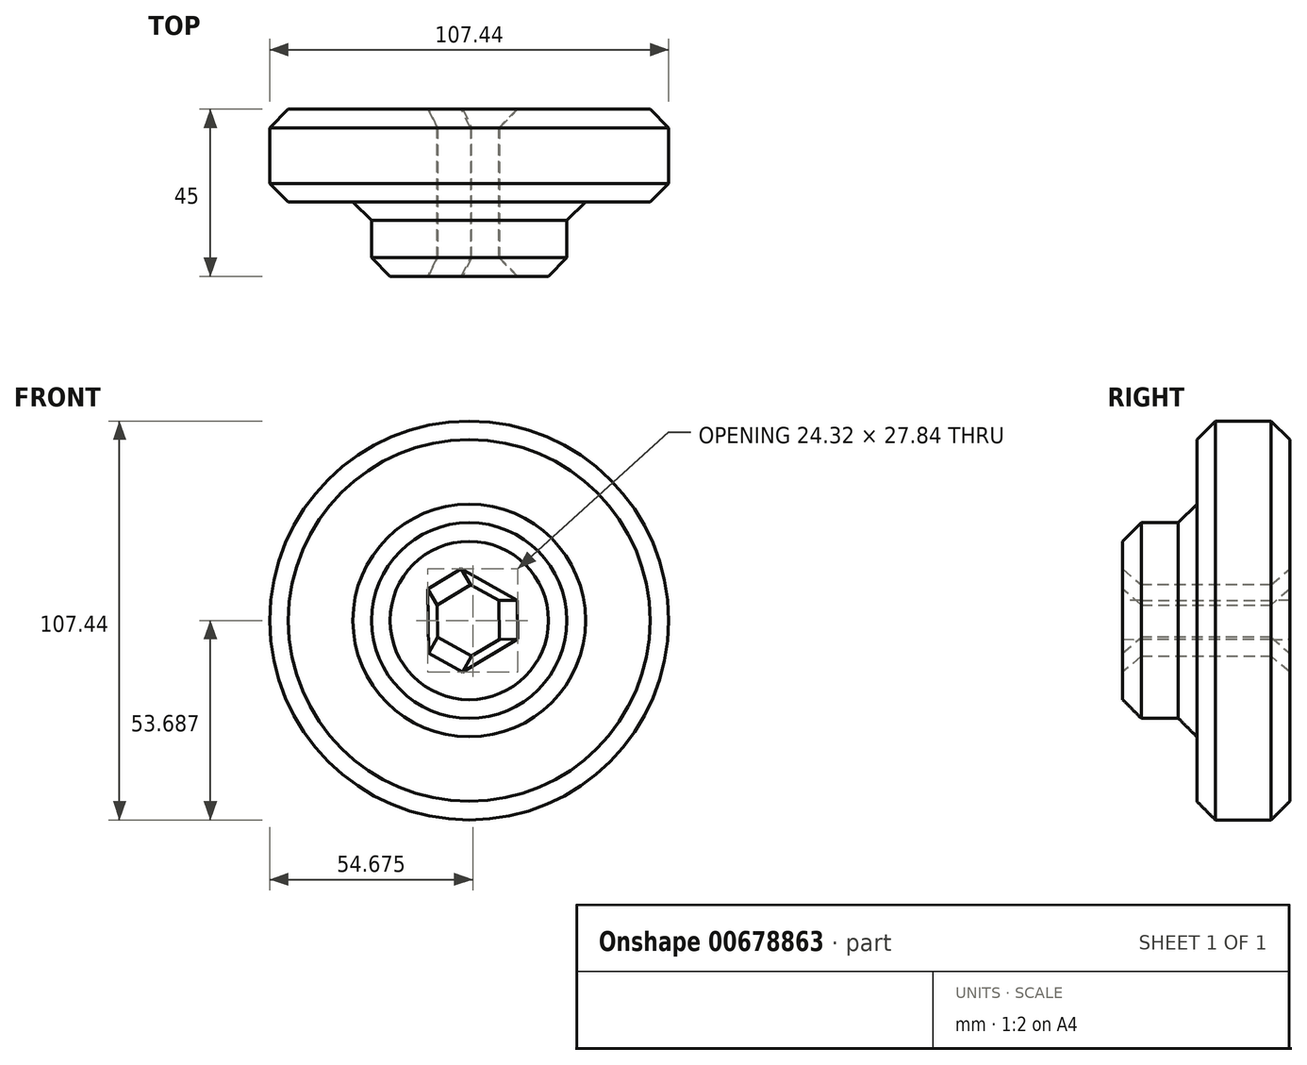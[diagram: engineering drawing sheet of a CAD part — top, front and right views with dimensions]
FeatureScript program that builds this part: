
annotation { "Feature Type Name" : "Feature", "Feature Type Description" : "" }
export const myFeature = defineFeature(function(context is Context, id is Id, definition is map)
    precondition{}
    {
        {
            var Q0;
            Q0=qCreatedBy(makeId("Front.planeOp"),FACE);
            var sketch = newSketch(context, id + "F0", { "sketchPlane" : qUnion([Q0])});
            skCircle(sketch, "E0", {"center": v(0, 0) * mm, "radius": 53.72 * mm});
            skCircle(sketch, "E1", {"center": v(0, 0) * mm, "radius": 58.67 * mm, "construction": true});
            skCircle(sketch, "E2", {"center": v(0, 0) * mm, "radius": 63.5 * mm, "construction": true});
            skLineSegment(sketch, "E3", {"start": v(0, 0) * mm, "end": v(0, 90.81) * mm, "construction": true});
            skLineSegment(sketch, "E4", {"start": v(0, 0) * mm, "end": v(-6.87, 104.81) * mm, "construction": true});
            skLineSegment(sketch, "E5", {"start": v(0, 58.67) * mm, "end": v(-81.02, 58.67) * mm, "construction": true});
            skLineSegment(sketch, "E6", {"start": v(0, 58.67) * mm, "end": v(-77.42, 30.5) * mm, "construction": true});
            skCircle(sketch, "E7", {"center": v(0, 0) * mm, "radius": 55.14 * mm, "construction": true});
            skCircle(sketch, "E8", {"center": v(0, 58.67) * mm, "radius": 14.6 * mm, "construction": true});
            skCircle(sketch, "E9", {"center": v(-13.72, 53.68) * mm, "radius": 14.6 * mm, "construction": true});
            skArc(sketch, "E10", {"start": v(0, 58.67) * mm, "mid": v(-1.21, 61.19) * mm, "end": v(-2.86, 63.44) * mm});
            skArc(sketch, "E11", {"start": v(0.88, 53.71) * mm, "mid": v(0.66, 56.23) * mm, "end": v(0, 58.67) * mm});
            skArc(sketch, "E12.MirrorCS", {"start": v(-7.88, 53.14) * mm, "mid": v(-8, 55.67) * mm, "end": v(-7.66, 58.17) * mm});
            skArc(sketch, "E13.MirrorCS", {"start": v(-7.66, 58.17) * mm, "mid": v(-6.79, 60.82) * mm, "end": v(-5.45, 63.27) * mm});
            skLineSegment(sketch, "E14", {"start": v(-5.45, 63.27) * mm, "end": v(-4.02, 61.3) * mm});
            skLineSegment(sketch, "E15", {"start": v(-4.02, 61.3) * mm, "end": v(-2.86, 63.44) * mm});
            skCircle(sketch, "E16", {"center": v(0, 0) * mm, "radius": 26.33 * mm});
            skCircle(sketch, "E17.cCircle", {"center": v(0, 0) * mm, "radius": 8.04 * mm, "construction": true});
            skLineSegment(sketch, "E17.0", {"start": v(-16.07, -0.25) * mm, "end": v(7.82, 14.04) * mm});
            skLineSegment(sketch, "E17.1", {"start": v(7.82, 14.04) * mm, "end": v(8.25, -13.8) * mm});
            skLineSegment(sketch, "E17.2", {"start": v(8.25, -13.8) * mm, "end": v(-16.07, -0.25) * mm});
            skPoint(sketch, "E17.0.midPoint", {"position": v(-4.12, 6.9) * mm});
            skSolve(sketch);
        }
        {
            var Q0;
            Q0=makeQuery(id+"F0.imprint","IMPRINT",FACE,{"disambiguationData":[TD([[makeQuery(id+"F0.imprint","IMPRINT",EDGE,{"derivedFrom":sQuery(id+"F0.wireOp",EDGE,"E10")}),1.0]])]});
            var Q1;
            {var subQ0=sQuery(id+"F0.wireOp",EDGE,"E0");var subQ1=makeQuery(id+"F0.imprint","INTERSECT",VERTEX,{"derivedFrom":[subQ0,sQuery(id+"F0.wireOp",EDGE,"E11")]});Q1=makeQuery(id+"F0.imprint","IMPRINT",FACE,{"disambiguationData":[TD([[makeQuery(id+"F0.imprint","IMPRINT",EDGE,{"disambiguationData":[TD([[subQ1,-1.0]])],"derivedFrom":subQ0}),1.0]])]});}
            extrude(context, id + "F1", {"entities" : qUnion([Q0, Q1]), "depth" : 25 * mm, "offsetDistance" : 25 * mm});
        }
        {
            var Q0;
            Q0=makeQuery(id+"F1.opExtrude","SWEPT_BODY",BODY,{"disambiguationData":[OSD([sQuery(id+"F0.wireOp",EDGE,"E0"),sQuery(id+"F0.wireOp",EDGE,"E10"),sQuery(id+"F0.wireOp",EDGE,"E11"),sQuery(id+"F0.wireOp",EDGE,"E12.MirrorCS"),sQuery(id+"F0.wireOp",EDGE,"E13.MirrorCS"),sQuery(id+"F0.wireOp",EDGE,"E14"),sQuery(id+"F0.wireOp",EDGE,"E15")])]});
            var Q1;
            Q1=makeQuery(id+"F1.opExtrude","SWEPT_FACE",FACE,{"disambiguationData":[OSD([sQuery(id+"F0.wireOp",EDGE,"E0")])]});
            circularPattern(context, id + "F2", {"entities" : qUnion([Q0]), "axis" : qUnion([Q1]), "angle" : 360 * degree, "instanceCount" : 12, "equalSpace" : true});
        }
        {
            var Q0;
            Q0=makeQuery(id+"F0.imprint","IMPRINT",FACE,{"disambiguationData":[TD([[makeQuery(id+"F0.imprint","IMPRINT",EDGE,{"derivedFrom":sQuery(id+"F0.wireOp",EDGE,"E16")}),1.0]])]});
            extrude(context, id + "F3", {"entities" : qUnion([Q0]), "operationType" : NewBodyOperationType.ADD, "depth" : 45 * mm, "offsetDistance" : 25 * mm});
        }
        {
            var Q0;
            Q0=makeQuery(id+"F3.opExtrude","SWEPT_FACE",FACE,{"disambiguationData":[OSD([sQuery(id+"F0.wireOp",EDGE,"E17.2")])]});
            var Q1;
            Q1=makeQuery(id+"F3.opExtrude","SWEPT_FACE",FACE,{"disambiguationData":[OSD([sQuery(id+"F0.wireOp",EDGE,"E17.1")])]});
            var Q2;
            Q2=makeQuery(id+"F3.opExtrude","SWEPT_FACE",FACE,{"disambiguationData":[OSD([sQuery(id+"F0.wireOp",EDGE,"E17.0")])]});
            var Q3;
            {var subQ5=sQuery(id+"F0.wireOp",EDGE,"E11");var subQ7=sQuery(id+"F0.wireOp",EDGE,"E0");Q3=makeQuery(id+"F3.boolean.opBoolean","SPLIT",FACE,{"disambiguationData":[TD([makeQuery(id+"F2.opPattern","COPY",FACE,{"derivedFrom":makeQuery(id+"F1.opExtrude","SWEPT_FACE",FACE,{"disambiguationData":[OSD([subQ5])]}),"instanceName":"19"})])],"derivedFrom":makeQuery(id+"F1.opExtrude","SWEPT_FACE",FACE,{"disambiguationData":[OSD([subQ7])]})});}
            var Q4;
            {var subQ5=sQuery(id+"F0.wireOp",EDGE,"E11");var subQ7=sQuery(id+"F0.wireOp",EDGE,"E0");Q4=makeQuery(id+"F3.boolean.opBoolean","SPLIT",FACE,{"disambiguationData":[TD([makeQuery(id+"F2.opPattern","COPY",FACE,{"derivedFrom":makeQuery(id+"F1.opExtrude","SWEPT_FACE",FACE,{"disambiguationData":[OSD([subQ5])]}),"instanceName":"20"})])],"derivedFrom":makeQuery(id+"F1.opExtrude","SWEPT_FACE",FACE,{"disambiguationData":[OSD([subQ7])]})});}
            var Q5;
            {var subQ0=sQuery(id+"F0.wireOp",EDGE,"E11");var subQ7=sQuery(id+"F0.wireOp",EDGE,"E0");Q5=makeQuery(id+"F3.boolean.opBoolean","SPLIT",FACE,{"disambiguationData":[TD([makeQuery(id+"F2.opPattern","COPY",FACE,{"derivedFrom":makeQuery(id+"F1.opExtrude","SWEPT_FACE",FACE,{"disambiguationData":[OSD([subQ0])]}),"instanceName":"21"})])],"derivedFrom":makeQuery(id+"F1.opExtrude","SWEPT_FACE",FACE,{"disambiguationData":[OSD([subQ7])]})});}
            var Q6;
            {var subQ5=sQuery(id+"F0.wireOp",EDGE,"E11");var subQ7=sQuery(id+"F0.wireOp",EDGE,"E0");Q6=makeQuery(id+"F3.boolean.opBoolean","SPLIT",FACE,{"disambiguationData":[TD([makeQuery(id+"F2.opPattern","COPY",FACE,{"derivedFrom":makeQuery(id+"F1.opExtrude","SWEPT_FACE",FACE,{"disambiguationData":[OSD([subQ5])]}),"instanceName":"22"})])],"derivedFrom":makeQuery(id+"F1.opExtrude","SWEPT_FACE",FACE,{"disambiguationData":[OSD([subQ7])]})});}
            var Q7;
            {var subQ4=sQuery(id+"F0.wireOp",EDGE,"E12.MirrorCS");var subQ7=sQuery(id+"F0.wireOp",EDGE,"E0");Q7=makeQuery(id+"F3.boolean.opBoolean","SPLIT",FACE,{"disambiguationData":[TD([makeQuery(id+"F1.opExtrude","SWEPT_FACE",FACE,{"disambiguationData":[OSD([subQ4])]})])],"derivedFrom":makeQuery(id+"F1.opExtrude","SWEPT_FACE",FACE,{"disambiguationData":[OSD([subQ7])]})});}
            var Q8;
            {var subQ5=sQuery(id+"F0.wireOp",EDGE,"E11");var subQ7=sQuery(id+"F0.wireOp",EDGE,"E0");Q8=makeQuery(id+"F3.boolean.opBoolean","SPLIT",FACE,{"disambiguationData":[TD([makeQuery(id+"F1.opExtrude","SWEPT_FACE",FACE,{"disambiguationData":[OSD([subQ5])]})])],"derivedFrom":makeQuery(id+"F1.opExtrude","SWEPT_FACE",FACE,{"disambiguationData":[OSD([subQ7])]})});}
            var Q9;
            {var subQ5=sQuery(id+"F0.wireOp",EDGE,"E11");var subQ7=sQuery(id+"F0.wireOp",EDGE,"E0");Q9=makeQuery(id+"F3.boolean.opBoolean","SPLIT",FACE,{"disambiguationData":[TD([makeQuery(id+"F2.opPattern","COPY",FACE,{"derivedFrom":makeQuery(id+"F1.opExtrude","SWEPT_FACE",FACE,{"disambiguationData":[OSD([subQ5])]}),"instanceName":"1"})])],"derivedFrom":makeQuery(id+"F1.opExtrude","SWEPT_FACE",FACE,{"disambiguationData":[OSD([subQ7])]})});}
            var Q10;
            {var subQ5=sQuery(id+"F0.wireOp",EDGE,"E11");var subQ7=sQuery(id+"F0.wireOp",EDGE,"E0");Q10=makeQuery(id+"F3.boolean.opBoolean","SPLIT",FACE,{"disambiguationData":[TD([makeQuery(id+"F2.opPattern","COPY",FACE,{"derivedFrom":makeQuery(id+"F1.opExtrude","SWEPT_FACE",FACE,{"disambiguationData":[OSD([subQ5])]}),"instanceName":"2"})])],"derivedFrom":makeQuery(id+"F1.opExtrude","SWEPT_FACE",FACE,{"disambiguationData":[OSD([subQ7])]})});}
            var Q11;
            {var subQ5=sQuery(id+"F0.wireOp",EDGE,"E11");var subQ7=sQuery(id+"F0.wireOp",EDGE,"E0");Q11=makeQuery(id+"F3.boolean.opBoolean","SPLIT",FACE,{"disambiguationData":[TD([makeQuery(id+"F2.opPattern","COPY",FACE,{"derivedFrom":makeQuery(id+"F1.opExtrude","SWEPT_FACE",FACE,{"disambiguationData":[OSD([subQ5])]}),"instanceName":"4"})])],"derivedFrom":makeQuery(id+"F1.opExtrude","SWEPT_FACE",FACE,{"disambiguationData":[OSD([subQ7])]})});}
            var Q12;
            {var subQ5=sQuery(id+"F0.wireOp",EDGE,"E11");var subQ7=sQuery(id+"F0.wireOp",EDGE,"E0");Q12=makeQuery(id+"F3.boolean.opBoolean","SPLIT",FACE,{"disambiguationData":[TD([makeQuery(id+"F2.opPattern","COPY",FACE,{"derivedFrom":makeQuery(id+"F1.opExtrude","SWEPT_FACE",FACE,{"disambiguationData":[OSD([subQ5])]}),"instanceName":"3"})])],"derivedFrom":makeQuery(id+"F1.opExtrude","SWEPT_FACE",FACE,{"disambiguationData":[OSD([subQ7])]})});}
            var Q13;
            {var subQ5=sQuery(id+"F0.wireOp",EDGE,"E11");var subQ7=sQuery(id+"F0.wireOp",EDGE,"E0");Q13=makeQuery(id+"F3.boolean.opBoolean","SPLIT",FACE,{"disambiguationData":[TD([makeQuery(id+"F2.opPattern","COPY",FACE,{"derivedFrom":makeQuery(id+"F1.opExtrude","SWEPT_FACE",FACE,{"disambiguationData":[OSD([subQ5])]}),"instanceName":"5"})])],"derivedFrom":makeQuery(id+"F1.opExtrude","SWEPT_FACE",FACE,{"disambiguationData":[OSD([subQ7])]})});}
            var Q14;
            {var subQ5=sQuery(id+"F0.wireOp",EDGE,"E11");var subQ7=sQuery(id+"F0.wireOp",EDGE,"E0");Q14=makeQuery(id+"F3.boolean.opBoolean","SPLIT",FACE,{"disambiguationData":[TD([makeQuery(id+"F2.opPattern","COPY",FACE,{"derivedFrom":makeQuery(id+"F1.opExtrude","SWEPT_FACE",FACE,{"disambiguationData":[OSD([subQ5])]}),"instanceName":"6"})])],"derivedFrom":makeQuery(id+"F1.opExtrude","SWEPT_FACE",FACE,{"disambiguationData":[OSD([subQ7])]})});}
            var Q15;
            {var subQ5=sQuery(id+"F0.wireOp",EDGE,"E11");var subQ7=sQuery(id+"F0.wireOp",EDGE,"E0");Q15=makeQuery(id+"F3.boolean.opBoolean","SPLIT",FACE,{"disambiguationData":[TD([makeQuery(id+"F2.opPattern","COPY",FACE,{"derivedFrom":makeQuery(id+"F1.opExtrude","SWEPT_FACE",FACE,{"disambiguationData":[OSD([subQ5])]}),"instanceName":"7"})])],"derivedFrom":makeQuery(id+"F1.opExtrude","SWEPT_FACE",FACE,{"disambiguationData":[OSD([subQ7])]})});}
            var Q16;
            {var subQ5=sQuery(id+"F0.wireOp",EDGE,"E11");var subQ7=sQuery(id+"F0.wireOp",EDGE,"E0");Q16=makeQuery(id+"F3.boolean.opBoolean","SPLIT",FACE,{"disambiguationData":[TD([makeQuery(id+"F2.opPattern","COPY",FACE,{"derivedFrom":makeQuery(id+"F1.opExtrude","SWEPT_FACE",FACE,{"disambiguationData":[OSD([subQ5])]}),"instanceName":"8"})])],"derivedFrom":makeQuery(id+"F1.opExtrude","SWEPT_FACE",FACE,{"disambiguationData":[OSD([subQ7])]})});}
            var Q17;
            {var subQ5=sQuery(id+"F0.wireOp",EDGE,"E11");var subQ7=sQuery(id+"F0.wireOp",EDGE,"E0");Q17=makeQuery(id+"F3.boolean.opBoolean","SPLIT",FACE,{"disambiguationData":[TD([makeQuery(id+"F2.opPattern","COPY",FACE,{"derivedFrom":makeQuery(id+"F1.opExtrude","SWEPT_FACE",FACE,{"disambiguationData":[OSD([subQ5])]}),"instanceName":"9"})])],"derivedFrom":makeQuery(id+"F1.opExtrude","SWEPT_FACE",FACE,{"disambiguationData":[OSD([subQ7])]})});}
            var Q18;
            {var subQ5=sQuery(id+"F0.wireOp",EDGE,"E11");var subQ7=sQuery(id+"F0.wireOp",EDGE,"E0");Q18=makeQuery(id+"F3.boolean.opBoolean","SPLIT",FACE,{"disambiguationData":[TD([makeQuery(id+"F2.opPattern","COPY",FACE,{"derivedFrom":makeQuery(id+"F1.opExtrude","SWEPT_FACE",FACE,{"disambiguationData":[OSD([subQ5])]}),"instanceName":"10"})])],"derivedFrom":makeQuery(id+"F1.opExtrude","SWEPT_FACE",FACE,{"disambiguationData":[OSD([subQ7])]})});}
            var Q19;
            {var subQ5=sQuery(id+"F0.wireOp",EDGE,"E11");var subQ7=sQuery(id+"F0.wireOp",EDGE,"E0");Q19=makeQuery(id+"F3.boolean.opBoolean","SPLIT",FACE,{"disambiguationData":[TD([makeQuery(id+"F2.opPattern","COPY",FACE,{"derivedFrom":makeQuery(id+"F1.opExtrude","SWEPT_FACE",FACE,{"disambiguationData":[OSD([subQ5])]}),"instanceName":"11"})])],"derivedFrom":makeQuery(id+"F1.opExtrude","SWEPT_FACE",FACE,{"disambiguationData":[OSD([subQ7])]})});}
            var Q20;
            {var subQ5=sQuery(id+"F0.wireOp",EDGE,"E11");var subQ7=sQuery(id+"F0.wireOp",EDGE,"E0");Q20=makeQuery(id+"F3.boolean.opBoolean","SPLIT",FACE,{"disambiguationData":[TD([makeQuery(id+"F2.opPattern","COPY",FACE,{"derivedFrom":makeQuery(id+"F1.opExtrude","SWEPT_FACE",FACE,{"disambiguationData":[OSD([subQ5])]}),"instanceName":"12"})])],"derivedFrom":makeQuery(id+"F1.opExtrude","SWEPT_FACE",FACE,{"disambiguationData":[OSD([subQ7])]})});}
            var Q21;
            {var subQ5=sQuery(id+"F0.wireOp",EDGE,"E11");var subQ7=sQuery(id+"F0.wireOp",EDGE,"E0");Q21=makeQuery(id+"F3.boolean.opBoolean","SPLIT",FACE,{"disambiguationData":[TD([makeQuery(id+"F2.opPattern","COPY",FACE,{"derivedFrom":makeQuery(id+"F1.opExtrude","SWEPT_FACE",FACE,{"disambiguationData":[OSD([subQ5])]}),"instanceName":"13"})])],"derivedFrom":makeQuery(id+"F1.opExtrude","SWEPT_FACE",FACE,{"disambiguationData":[OSD([subQ7])]})});}
            var Q22;
            {var subQ5=sQuery(id+"F0.wireOp",EDGE,"E11");var subQ7=sQuery(id+"F0.wireOp",EDGE,"E0");Q22=makeQuery(id+"F3.boolean.opBoolean","SPLIT",FACE,{"disambiguationData":[TD([makeQuery(id+"F2.opPattern","COPY",FACE,{"derivedFrom":makeQuery(id+"F1.opExtrude","SWEPT_FACE",FACE,{"disambiguationData":[OSD([subQ5])]}),"instanceName":"14"})])],"derivedFrom":makeQuery(id+"F1.opExtrude","SWEPT_FACE",FACE,{"disambiguationData":[OSD([subQ7])]})});}
            var Q23;
            {var subQ5=sQuery(id+"F0.wireOp",EDGE,"E11");var subQ7=sQuery(id+"F0.wireOp",EDGE,"E0");Q23=makeQuery(id+"F3.boolean.opBoolean","SPLIT",FACE,{"disambiguationData":[TD([makeQuery(id+"F2.opPattern","COPY",FACE,{"derivedFrom":makeQuery(id+"F1.opExtrude","SWEPT_FACE",FACE,{"disambiguationData":[OSD([subQ5])]}),"instanceName":"15"})])],"derivedFrom":makeQuery(id+"F1.opExtrude","SWEPT_FACE",FACE,{"disambiguationData":[OSD([subQ7])]})});}
            var Q24;
            {var subQ5=sQuery(id+"F0.wireOp",EDGE,"E11");var subQ7=sQuery(id+"F0.wireOp",EDGE,"E0");Q24=makeQuery(id+"F3.boolean.opBoolean","SPLIT",FACE,{"disambiguationData":[TD([makeQuery(id+"F2.opPattern","COPY",FACE,{"derivedFrom":makeQuery(id+"F1.opExtrude","SWEPT_FACE",FACE,{"disambiguationData":[OSD([subQ5])]}),"instanceName":"16"})])],"derivedFrom":makeQuery(id+"F1.opExtrude","SWEPT_FACE",FACE,{"disambiguationData":[OSD([subQ7])]})});}
            var Q25;
            {var subQ5=sQuery(id+"F0.wireOp",EDGE,"E11");var subQ7=sQuery(id+"F0.wireOp",EDGE,"E0");Q25=makeQuery(id+"F3.boolean.opBoolean","SPLIT",FACE,{"disambiguationData":[TD([makeQuery(id+"F2.opPattern","COPY",FACE,{"derivedFrom":makeQuery(id+"F1.opExtrude","SWEPT_FACE",FACE,{"disambiguationData":[OSD([subQ5])]}),"instanceName":"17"})])],"derivedFrom":makeQuery(id+"F1.opExtrude","SWEPT_FACE",FACE,{"disambiguationData":[OSD([subQ7])]})});}
            var Q26;
            {var subQ5=sQuery(id+"F0.wireOp",EDGE,"E11");var subQ7=sQuery(id+"F0.wireOp",EDGE,"E0");Q26=makeQuery(id+"F3.boolean.opBoolean","SPLIT",FACE,{"disambiguationData":[TD([makeQuery(id+"F2.opPattern","COPY",FACE,{"derivedFrom":makeQuery(id+"F1.opExtrude","SWEPT_FACE",FACE,{"disambiguationData":[OSD([subQ5])]}),"instanceName":"18"})])],"derivedFrom":makeQuery(id+"F1.opExtrude","SWEPT_FACE",FACE,{"disambiguationData":[OSD([subQ7])]})});}
            var Q27;
            Q27=makeQuery(id+"F3.opExtrude","SWEPT_FACE",FACE,{"disambiguationData":[OSD([sQuery(id+"F0.wireOp",EDGE,"E16")])]});
            chamfer(context, id + "F4", {"entities" : qUnion([Q0, Q1, Q2, Q3, Q4, Q5, Q6, Q7, Q8, Q9, Q10, Q11, Q12, Q13, Q14, Q15, Q16, Q17, Q18, Q19, Q20, Q21, Q22, Q23, Q24, Q25, Q26, Q27]), "width" : 5 * mm, "tangentPropagation" : true});
        }
    });
